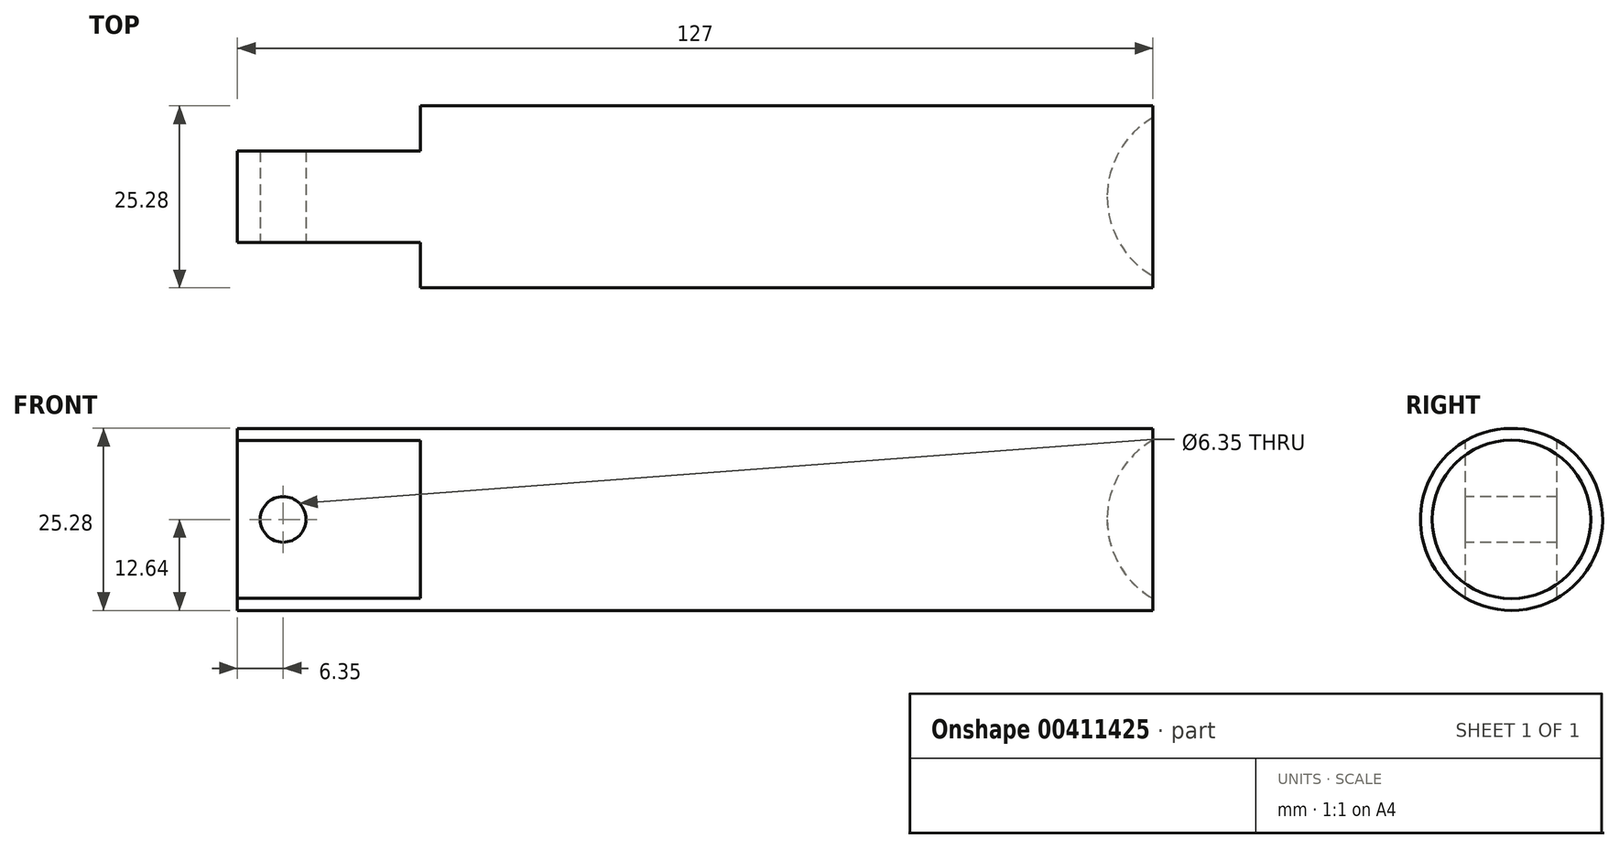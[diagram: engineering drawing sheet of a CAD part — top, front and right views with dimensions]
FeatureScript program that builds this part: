
annotation { "Feature Type Name" : "Feature", "Feature Type Description" : "" }
export const myFeature = defineFeature(function(context is Context, id is Id, definition is map)
    precondition{}
    {
        {
            var Q0;
            Q0=qCreatedBy(makeId("Right.planeOp"),FACE);
            var sketch = newSketch(context, id + "F0", { "sketchPlane" : qUnion([Q0])});
            skCircle(sketch, "E0", {"center": v(0, 0) * mm, "radius": 12.64 * mm});
            skSolve(sketch);
        }
        {
            var Q0;
            Q0 = qSketchRegion(id + "F0", true);
            extrude(context, id + "F1", {"entities" : qUnion([Q0]), "depth" : 127 * mm});
        }
        {
            var Q0;
            Q0=qCreatedBy(makeId("Top.planeOp"),FACE);
            var sketch = newSketch(context, id + "F2", { "sketchPlane" : qUnion([Q0])});
            skLineSegment(sketch, "E1.bottom", {"start": v(0, 18.14) * mm, "end": v(25.4, 18.14) * mm});
            skLineSegment(sketch, "E1.top", {"start": v(0, 6.35) * mm, "end": v(25.4, 6.35) * mm});
            skLineSegment(sketch, "E1.left", {"start": v(0, 18.14) * mm, "end": v(0, 6.35) * mm});
            skLineSegment(sketch, "E1.right", {"start": v(25.4, 18.14) * mm, "end": v(25.4, 6.35) * mm});
            skLineSegment(sketch, "E2.bottom", {"start": v(0, -6.35) * mm, "end": v(25.4, -6.35) * mm});
            skLineSegment(sketch, "E2.top", {"start": v(0, -18.82) * mm, "end": v(25.4, -18.82) * mm});
            skLineSegment(sketch, "E2.left", {"start": v(0, -6.35) * mm, "end": v(0, -18.82) * mm});
            skLineSegment(sketch, "E2.right", {"start": v(25.4, -6.35) * mm, "end": v(25.4, -18.82) * mm});
            skSolve(sketch);
        }
        {
            var Q0;
            Q0 = qSketchRegion(id + "F2", true);
            extrude(context, id + "F3", {"entities" : qUnion([Q0]), "operationType" : NewBodyOperationType.REMOVE, "oppositeDirection" : true, "depth" : 25.4 * mm, "hasSecondDirection" : true, "secondDirectionOppositeDirection" : false, "secondDirectionDepth" : 25.4 * mm});
        }
        {
            var Q0;
            Q0=makeQuery(id+"F3.boolean.opBoolean","COPY",FACE,{"derivedFrom":makeQuery(id+"F3.opExtrude","SWEPT_FACE",FACE,{"disambiguationData":[OSD([sQuery(id+"F2.wireOp",EDGE,"E2.bottom")])]})});
            var sketch = newSketch(context, id + "F4", { "sketchPlane" : qUnion([Q0])});
            skCircle(sketch, "E3", {"center": v(6.35, 0) * mm, "radius": 3.18 * mm});
            skSolve(sketch);
        }
        {
            var Q0;
            Q0 = qSketchRegion(id + "F4", true);
            extrude(context, id + "F5", {"entities" : qUnion([Q0]), "operationType" : NewBodyOperationType.REMOVE, "oppositeDirection" : true, "depth" : 25.4 * mm});
        }
        {
            var Q0;
            Q0=qCreatedBy(makeId("Front.planeOp"),FACE);
            var sketch = newSketch(context, id + "F6", { "sketchPlane" : qUnion([Q0])});
            skArc(sketch, "E4", {"start": v(146.05, 0) * mm, "mid": v(133.35, 12.7) * mm, "end": v(120.65, 0) * mm});
            skLineSegment(sketch, "E5", {"start": v(120.65, 0) * mm, "end": v(146.05, 0) * mm});
            skSolve(sketch);
        }
        {
            var Q0;
            Q0=makeQuery(id+"F6.imprint","IMPRINT",FACE,{"disambiguationData":[TD([[makeQuery(id+"F6.imprint","IMPRINT",EDGE,{"derivedFrom":sQuery(id+"F6.wireOp",EDGE,"E4")}),1.0]])]});
            var Q1;
            Q1=sQuery(id+"F6.wireOp",EDGE,"E5");
            revolve(context, id + "F7", {"operationType" : NewBodyOperationType.REMOVE, "entities" : qUnion([Q0]), "axis" : qUnion([Q1]), "revolveType" : RevolveType.FULL, "oppositeDirection" : true});
        }
    });
